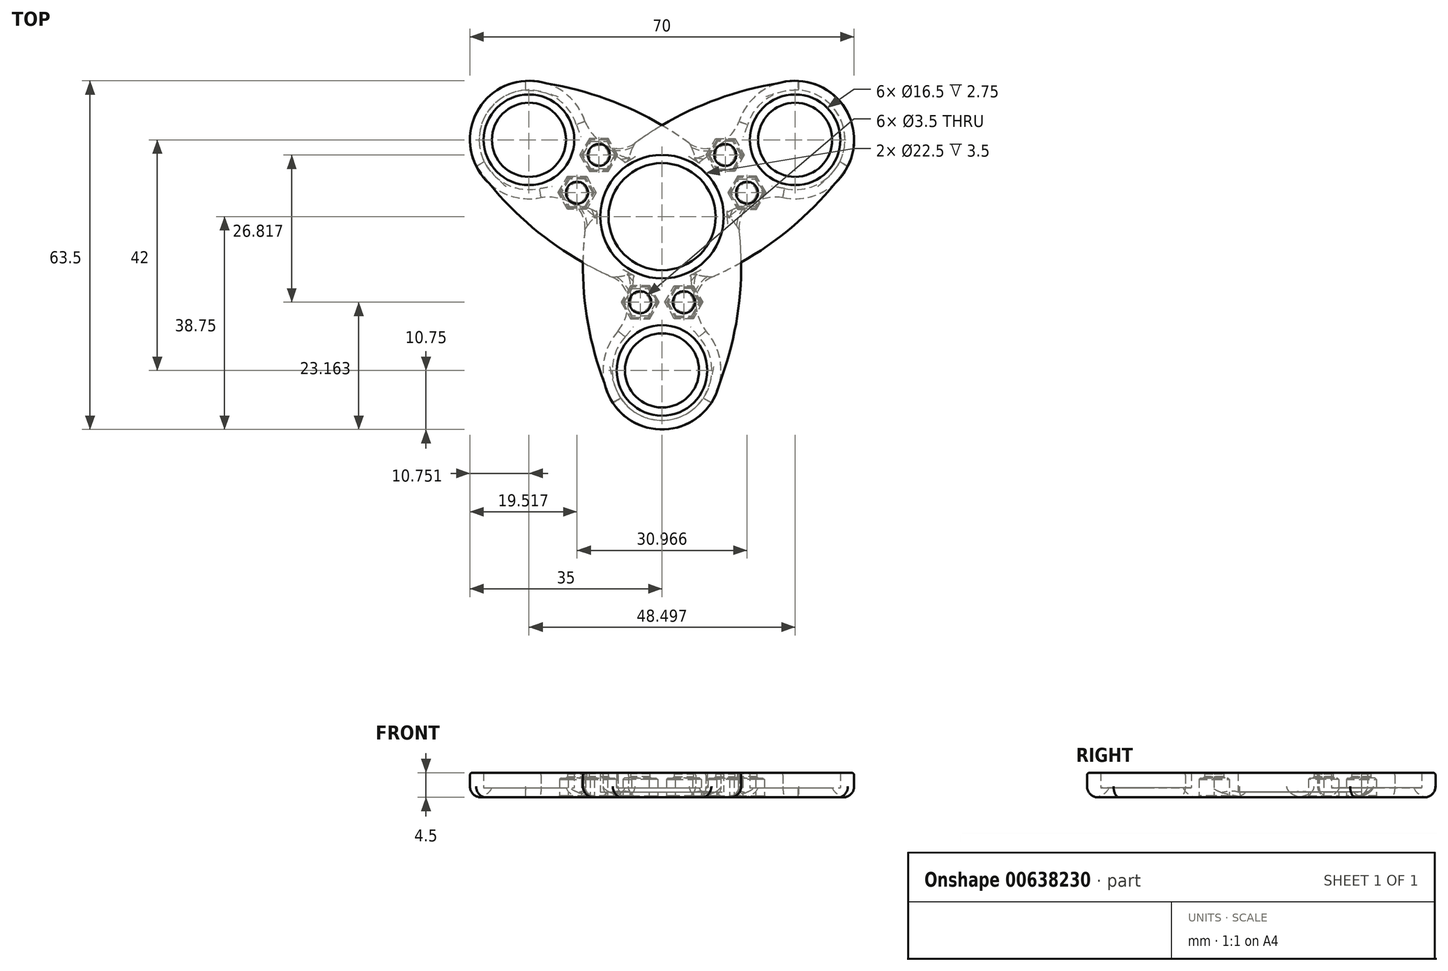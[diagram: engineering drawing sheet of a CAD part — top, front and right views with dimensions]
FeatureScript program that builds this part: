
annotation { "Feature Type Name" : "Feature", "Feature Type Description" : "" }
export const myFeature = defineFeature(function(context is Context, id is Id, definition is map)
    precondition{}
    {
        {
            assignVariable(context, id + "F0", {"name" : "OuterBearingHeight", "anyValue" : 5});
        }
        {
            assignVariable(context, id + "F1", {"name" : "CenterBearingHeight", "anyValue" : 7});
        }
        {
            var Q0;
            Q0=qCreatedBy(makeId("Top.planeOp"),FACE);
            var sketch = newSketch(context, id + "F2", { "sketchPlane" : qUnion([Q0])});
            skCircle(sketch, "E0", {"center": v(0, 0) * mm, "radius": 11.25 * mm});
            skCircle(sketch, "E1", {"center": v(0, 0) * mm, "radius": 9.75 * mm});
            skCircle(sketch, "E2", {"center": v(0, -28) * mm, "radius": 8.25 * mm});
            skCircle(sketch, "E3", {"center": v(0, -28) * mm, "radius": 6.75 * mm});
            skCircle(sketch, "E4", {"center": v(0, 0) * mm, "radius": 13.75 * mm});
            skCircle(sketch, "E5", {"center": v(0, -28) * mm, "radius": 10.75 * mm});
            skArc(sketch, "E6", {"start": v(-13.75, 0) * mm, "mid": v(-13.84, -17.29) * mm, "end": v(-9, -33.88) * mm});
            skArc(sketch, "E7", {"start": v(6.75, -11.98) * mm, "mid": v(6.2, -16.57) * mm, "end": v(8, -20.82) * mm});
            skPoint(sketch, "E8.center", {"position": v(0.04, 0.07) * mm});
            skCircle(sketch, "E9.cCircle", {"center": v(-3.97, -15.59) * mm, "radius": 2.75 * mm, "construction": true});
            skLineSegment(sketch, "E9.0", {"start": v(-2.38, -18.34) * mm, "end": v(-5.56, -18.34) * mm});
            skLineSegment(sketch, "E9.1", {"start": v(-5.56, -18.34) * mm, "end": v(-7.14, -15.59) * mm});
            skLineSegment(sketch, "E9.2", {"start": v(-7.14, -15.59) * mm, "end": v(-5.56, -12.84) * mm});
            skLineSegment(sketch, "E9.3", {"start": v(-5.56, -12.84) * mm, "end": v(-2.38, -12.84) * mm});
            skLineSegment(sketch, "E9.4", {"start": v(-2.38, -12.84) * mm, "end": v(-0.8, -15.59) * mm});
            skLineSegment(sketch, "E9.5", {"start": v(-0.8, -15.59) * mm, "end": v(-2.38, -18.34) * mm});
            skPoint(sketch, "E9.0.midPoint", {"position": v(-3.97, -18.34) * mm});
            skLineSegment(sketch, "E10", {"start": v(-3.97, -15.59) * mm, "end": v(-3.97, -13.16) * mm, "construction": true});
            skLineSegment(sketch, "E11", {"start": v(-3.97, -15.59) * mm, "end": v(-3.97, -18) * mm, "construction": true});
            skLineSegment(sketch, "E12", {"start": v(-3.97, -15.59) * mm, "end": v(-14.05, -15.59) * mm, "construction": true});
            skLineSegment(sketch, "E13", {"start": v(-3.97, -15.59) * mm, "end": v(6.12, -15.59) * mm, "construction": true});
            skCircle(sketch, "E14", {"center": v(-3.97, -15.59) * mm, "radius": 1.75 * mm});
            skArc(sketch, "E15.1.0", {"start": v(7, 11.84) * mm, "mid": v(11.25, 13.65) * mm, "end": v(14.03, 17.34) * mm});
            skCircle(sketch, "E15.1.1", {"center": v(24.25, 14) * mm, "radius": 10.75 * mm});
            skCircle(sketch, "E15.1.2", {"center": v(24.25, 14) * mm, "radius": 8.25 * mm});
            skCircle(sketch, "E15.1.3", {"center": v(24.25, 14) * mm, "radius": 6.75 * mm});
            skArc(sketch, "E15.1.4", {"start": v(6.88, -11.9) * mm, "mid": v(21.89, -3.34) * mm, "end": v(33.84, 9.15) * mm});
            skLineSegment(sketch, "E15.1.5", {"start": v(13.9, 7.1) * mm, "end": v(17.07, 7.1) * mm});
            skLineSegment(sketch, "E15.1.6", {"start": v(12.3, 4.36) * mm, "end": v(13.9, 7.1) * mm});
            skLineSegment(sketch, "E15.1.7", {"start": v(13.9, 1.6) * mm, "end": v(12.3, 4.36) * mm});
            skLineSegment(sketch, "E15.1.8", {"start": v(17.07, 1.6) * mm, "end": v(13.9, 1.6) * mm});
            skLineSegment(sketch, "E15.1.9", {"start": v(18.66, 4.36) * mm, "end": v(17.07, 1.6) * mm});
            skLineSegment(sketch, "E15.1.10", {"start": v(17.07, 7.1) * mm, "end": v(18.66, 4.36) * mm});
            skCircle(sketch, "E15.1.11", {"center": v(15.48, 4.36) * mm, "radius": 1.75 * mm});
            skArc(sketch, "E15.2.0", {"start": v(-13.75, 0.14) * mm, "mid": v(-17.45, 2.91) * mm, "end": v(-22.03, 3.48) * mm});
            skCircle(sketch, "E15.2.1", {"center": v(-24.25, 14) * mm, "radius": 10.75 * mm});
            skCircle(sketch, "E15.2.2", {"center": v(-24.25, 14) * mm, "radius": 8.25 * mm});
            skCircle(sketch, "E15.2.3", {"center": v(-24.25, 14) * mm, "radius": 6.75 * mm});
            skArc(sketch, "E15.2.4", {"start": v(6.87, 11.9) * mm, "mid": v(-8.05, 20.63) * mm, "end": v(-24.84, 24.73) * mm});
            skLineSegment(sketch, "E15.2.5", {"start": v(-13.1, 8.48) * mm, "end": v(-14.7, 11.23) * mm});
            skLineSegment(sketch, "E15.2.6", {"start": v(-9.93, 8.48) * mm, "end": v(-13.1, 8.48) * mm});
            skLineSegment(sketch, "E15.2.7", {"start": v(-8.34, 11.23) * mm, "end": v(-9.93, 8.48) * mm});
            skLineSegment(sketch, "E15.2.8", {"start": v(-9.93, 13.98) * mm, "end": v(-8.34, 11.23) * mm});
            skLineSegment(sketch, "E15.2.9", {"start": v(-13.1, 13.98) * mm, "end": v(-9.93, 13.98) * mm});
            skLineSegment(sketch, "E15.2.10", {"start": v(-14.7, 11.23) * mm, "end": v(-13.1, 13.98) * mm});
            skCircle(sketch, "E15.2.11", {"center": v(-11.51, 11.23) * mm, "radius": 1.75 * mm});
            skSolve(sketch);
        }
        {
            var Q0;
            {var subQ0=sQuery(id+"F2.wireOp",EDGE,"E9.1");Q0=makeQuery(id+"F2.imprint","IMPRINT",FACE,{"disambiguationData":[TD([[makeQuery(id+"F2.imprint","IMPRINT",EDGE,{"derivedFrom":subQ0}),1.0]])]});}
            var Q1;
            {var subQ5=sQuery(id+"F2.wireOp",EDGE,"E7");Q1=makeQuery(id+"F2.imprint","IMPRINT",FACE,{"disambiguationData":[TD([[makeQuery(id+"F2.imprint","IMPRINT",EDGE,{"derivedFrom":subQ5}),-1.0]])]});}
            var Q2;
            {var subQ0=sQuery(id+"F2.wireOp",EDGE,"E15.1.8");Q2=makeQuery(id+"F2.imprint","IMPRINT",FACE,{"disambiguationData":[TD([[makeQuery(id+"F2.imprint","IMPRINT",EDGE,{"derivedFrom":subQ0}),1.0]])]});}
            var Q3;
            Q3=makeQuery(id+"F2.imprint","IMPRINT",FACE,{"disambiguationData":[TD([[makeQuery(id+"F2.imprint","IMPRINT",EDGE,{"derivedFrom":sQuery(id+"F2.wireOp",EDGE,"E0")}),-1.0]])]});
            var Q4;
            {var subQ1=sQuery(id+"F2.wireOp",EDGE,"E15.1.0");Q4=makeQuery(id+"F2.imprint","IMPRINT",FACE,{"disambiguationData":[TD([[makeQuery(id+"F2.imprint","IMPRINT",EDGE,{"derivedFrom":subQ1}),-1.0]])]});}
            var Q5;
            {var subQ0=sQuery(id+"F2.wireOp",EDGE,"E15.2.8");Q5=makeQuery(id+"F2.imprint","IMPRINT",FACE,{"disambiguationData":[TD([[makeQuery(id+"F2.imprint","IMPRINT",EDGE,{"derivedFrom":subQ0}),1.0]])]});}
            var Q6;
            Q6=makeQuery(id+"F2.imprint","IMPRINT",FACE,{"disambiguationData":[TD([[makeQuery(id+"F2.imprint","IMPRINT",EDGE,{"derivedFrom":sQuery(id+"F2.wireOp",EDGE,"E15.2.2")}),-1.0]])]});
            var Q7;
            Q7=makeQuery(id+"F2.imprint","IMPRINT",FACE,{"disambiguationData":[TD([[makeQuery(id+"F2.imprint","IMPRINT",EDGE,{"derivedFrom":sQuery(id+"F2.wireOp",EDGE,"E15.1.2")}),-1.0]])]});
            var Q8;
            {var subQ1=sQuery(id+"F2.wireOp",EDGE,"E15.2.0");Q8=makeQuery(id+"F2.imprint","IMPRINT",FACE,{"disambiguationData":[TD([[makeQuery(id+"F2.imprint","IMPRINT",EDGE,{"derivedFrom":subQ1}),-1.0]])]});}
            var Q9;
            Q9=makeQuery(id+"F2.imprint","IMPRINT",FACE,{"disambiguationData":[TD([[makeQuery(id+"F2.imprint","IMPRINT",EDGE,{"derivedFrom":sQuery(id+"F2.wireOp",EDGE,"E2")}),-1.0]])]});
            extrude(context, id + "F3", {"entities" : qUnion([Q0, Q1, Q2, Q3, Q4, Q5, Q6, Q7, Q8, Q9]), "depth" : ((getVariable(context, 'CenterBearingHeight') / 2) + 1) * mm, "offsetDistance" : 25 * mm});
        }
        {
            var Q0;
            Q0=makeQuery(id+"F2.imprint","IMPRINT",FACE,{"disambiguationData":[TD([[makeQuery(id+"F2.imprint","IMPRINT",EDGE,{"derivedFrom":sQuery(id+"F2.wireOp",EDGE,"E15.2.2")}),1.0]])]});
            var Q1;
            Q1=makeQuery(id+"F2.imprint","IMPRINT",FACE,{"disambiguationData":[TD([[makeQuery(id+"F2.imprint","IMPRINT",EDGE,{"derivedFrom":sQuery(id+"F2.wireOp",EDGE,"E15.1.2")}),1.0]])]});
            var Q2;
            Q2=makeQuery(id+"F2.imprint","IMPRINT",FACE,{"disambiguationData":[TD([[makeQuery(id+"F2.imprint","IMPRINT",EDGE,{"derivedFrom":sQuery(id+"F2.wireOp",EDGE,"E2")}),1.0]])]});
            extrude(context, id + "F4", {"entities" : qUnion([Q0, Q1, Q2]), "operationType" : NewBodyOperationType.ADD, "depth" : (((getVariable(context, 'CenterBearingHeight') / 2) + .75) - getVariable(context, 'OuterBearingHeight') / 2) * mm, "offsetDistance" : 25 * mm});
        }
        {
            var Q0;
            {var subQ0=sQuery(id+"F2.wireOp",EDGE,"E9.1");Q0=makeQuery(id+"F2.imprint","IMPRINT",FACE,{"disambiguationData":[TD([[makeQuery(id+"F2.imprint","IMPRINT",EDGE,{"derivedFrom":subQ0}),-1.0]])]});}
            var Q1;
            {var subQ0=sQuery(id+"F2.wireOp",EDGE,"E9.3");var subQ1=sQuery(id+"F2.wireOp",EDGE,"E4");var subQ2=makeQuery(id+"F2.imprint","INTERSECT",VERTEX,{"derivedFrom":[subQ1,subQ0]});Q1=makeQuery(id+"F2.imprint","IMPRINT",FACE,{"disambiguationData":[TD([[makeQuery(id+"F2.imprint","IMPRINT",EDGE,{"disambiguationData":[TD([[subQ2,-1.0]])],"derivedFrom":subQ1}),1.0]])]});}
            var Q2;
            {var subQ0=sQuery(id+"F2.wireOp",EDGE,"E9.5");var subQ1=sQuery(id+"F2.wireOp",EDGE,"E5");var subQ2=makeQuery(id+"F2.imprint","INTERSECT",VERTEX,{"derivedFrom":[subQ1,subQ0]});Q2=makeQuery(id+"F2.imprint","IMPRINT",FACE,{"disambiguationData":[TD([[makeQuery(id+"F2.imprint","IMPRINT",EDGE,{"disambiguationData":[TD([[subQ2,-1.0]])],"derivedFrom":subQ1}),1.0]])]});}
            var Q3;
            {var subQ0=sQuery(id+"F2.wireOp",EDGE,"E15.2.7");var subQ1=sQuery(id+"F2.wireOp",EDGE,"E4");var subQ2=makeQuery(id+"F2.imprint","INTERSECT",VERTEX,{"derivedFrom":[subQ1,subQ0]});Q3=makeQuery(id+"F2.imprint","IMPRINT",FACE,{"disambiguationData":[TD([[makeQuery(id+"F2.imprint","IMPRINT",EDGE,{"disambiguationData":[TD([[subQ2,-1.0]])],"derivedFrom":subQ1}),1.0]])]});}
            var Q4;
            {var subQ11=sQuery(id+"F2.wireOp",EDGE,"E15.2.8");Q4=makeQuery(id+"F2.imprint","IMPRINT",FACE,{"disambiguationData":[TD([[makeQuery(id+"F2.imprint","IMPRINT",EDGE,{"derivedFrom":subQ11}),-1.0]])]});}
            var Q5;
            {var subQ0=sQuery(id+"F2.wireOp",EDGE,"E15.2.5");var subQ1=sQuery(id+"F2.wireOp",EDGE,"E15.2.1");var subQ2=makeQuery(id+"F2.imprint","INTERSECT",VERTEX,{"derivedFrom":[subQ1,subQ0]});Q5=makeQuery(id+"F2.imprint","IMPRINT",FACE,{"disambiguationData":[TD([[makeQuery(id+"F2.imprint","IMPRINT",EDGE,{"disambiguationData":[TD([[subQ2,-1.0]])],"derivedFrom":subQ1}),1.0]])]});}
            var Q6;
            {var subQ11=sQuery(id+"F2.wireOp",EDGE,"E15.1.8");Q6=makeQuery(id+"F2.imprint","IMPRINT",FACE,{"disambiguationData":[TD([[makeQuery(id+"F2.imprint","IMPRINT",EDGE,{"derivedFrom":subQ11}),-1.0]])]});}
            var Q7;
            {var subQ0=sQuery(id+"F2.wireOp",EDGE,"E15.1.5");var subQ1=sQuery(id+"F2.wireOp",EDGE,"E15.1.1");var subQ2=makeQuery(id+"F2.imprint","INTERSECT",VERTEX,{"derivedFrom":[subQ1,subQ0]});Q7=makeQuery(id+"F2.imprint","IMPRINT",FACE,{"disambiguationData":[TD([[makeQuery(id+"F2.imprint","IMPRINT",EDGE,{"disambiguationData":[TD([[subQ2,-1.0]])],"derivedFrom":subQ1}),1.0]])]});}
            var Q8;
            {var subQ0=sQuery(id+"F2.wireOp",EDGE,"E15.1.6");var subQ1=sQuery(id+"F2.wireOp",EDGE,"E4");var subQ2=makeQuery(id+"F2.imprint","INTERSECT",VERTEX,{"derivedFrom":[subQ1,subQ0]});Q8=makeQuery(id+"F2.imprint","IMPRINT",FACE,{"disambiguationData":[TD([[makeQuery(id+"F2.imprint","IMPRINT",EDGE,{"disambiguationData":[TD([[subQ2,1.0]])],"derivedFrom":subQ1}),1.0]])]});}
            extrude(context, id + "F5", {"entities" : qUnion([Q0, Q1, Q2, Q3, Q4, Q5, Q6, Q7, Q8]), "operationType" : NewBodyOperationType.ADD, "depth" : ((getVariable(context, 'CenterBearingHeight') / 2) + 1) * mm, "offsetDistance" : 25 * mm, "hasSecondDirection" : true, "secondDirectionOppositeDirection" : false, "secondDirectionDepth" : 3.5 * mm});
        }
        {
            var Q0;
            Q0=makeQuery(id+"F2.imprint","IMPRINT",FACE,{"disambiguationData":[TD([[makeQuery(id+"F2.imprint","IMPRINT",EDGE,{"derivedFrom":sQuery(id+"F2.wireOp",EDGE,"E0")}),1.0]])]});
            extrude(context, id + "F6", {"entities" : qUnion([Q0]), "operationType" : NewBodyOperationType.ADD, "depth" : 1 * mm, "offsetDistance" : 25 * mm});
        }
        {
            var Q0;
            Q0=makeQuery(id+"F3.opExtrude","CAP_EDGE",EDGE,{"disambiguationData":[OSD([sQuery(id+"F2.wireOp",EDGE,"E15.1.1")])],"isStart":true});
            var Q1;
            Q1=makeQuery(id+"F3.opExtrude","CAP_EDGE",EDGE,{"disambiguationData":[OSD([sQuery(id+"F2.wireOp",EDGE,"E15.1.4")])],"isStart":true});
            var Q2;
            Q2=makeQuery(id+"F3.opExtrude","CAP_EDGE",EDGE,{"disambiguationData":[OSD([sQuery(id+"F2.wireOp",EDGE,"E7")])],"isStart":true});
            var Q3;
            Q3=makeQuery(id+"F3.opExtrude","CAP_EDGE",EDGE,{"disambiguationData":[OSD([sQuery(id+"F2.wireOp",EDGE,"E5")])],"isStart":true});
            var Q4;
            Q4=makeQuery(id+"F3.opExtrude","CAP_EDGE",EDGE,{"disambiguationData":[OSD([sQuery(id+"F2.wireOp",EDGE,"E6")])],"isStart":true});
            var Q5;
            Q5=makeQuery(id+"F3.opExtrude","CAP_EDGE",EDGE,{"disambiguationData":[OSD([sQuery(id+"F2.wireOp",EDGE,"E15.2.0")])],"isStart":true});
            var Q6;
            Q6=makeQuery(id+"F3.opExtrude","CAP_EDGE",EDGE,{"disambiguationData":[OSD([sQuery(id+"F2.wireOp",EDGE,"E15.2.1")])],"isStart":true});
            var Q7;
            Q7=makeQuery(id+"F3.opExtrude","CAP_EDGE",EDGE,{"disambiguationData":[OSD([sQuery(id+"F2.wireOp",EDGE,"E15.2.4")])],"isStart":true});
            var Q8;
            Q8=makeQuery(id+"F3.opExtrude","CAP_EDGE",EDGE,{"disambiguationData":[OSD([sQuery(id+"F2.wireOp",EDGE,"E15.1.0")])],"isStart":true});
            var Q9;
            {var subQ0=sQuery(id+"F2.wireOp",EDGE,"E4");Q9=makeQuery(id+"F3.opExtrude","CAP_EDGE",EDGE,{"disambiguationData":[OSD([subQ0]),TDD([makeQuery(id+"F2.imprint","IMPRINT",EDGE,{"disambiguationData":[TD([[makeQuery(id+"F2.imprint","INTERSECT",VERTEX,{"derivedFrom":[subQ0,sQuery(id+"F2.wireOp",EDGE,"E15.1.0")]}),-1.0]])],"derivedFrom":subQ0})])],"isStart":true});}
            var Q10;
            {var subQ0=sQuery(id+"F2.wireOp",EDGE,"E4");Q10=makeQuery(id+"F3.opExtrude","CAP_EDGE",EDGE,{"disambiguationData":[OSD([subQ0]),TDD([makeQuery(id+"F2.imprint","IMPRINT",EDGE,{"disambiguationData":[TD([[makeQuery(id+"F2.imprint","INTERSECT",VERTEX,{"derivedFrom":[subQ0,sQuery(id+"F2.wireOp",EDGE,"E6")]}),1.0]])],"derivedFrom":subQ0})])],"isStart":true});}
            var Q11;
            {var subQ0=sQuery(id+"F2.wireOp",EDGE,"E4");Q11=makeQuery(id+"F3.opExtrude","CAP_EDGE",EDGE,{"disambiguationData":[OSD([subQ0]),TDD([makeQuery(id+"F2.imprint","IMPRINT",EDGE,{"disambiguationData":[TD([[makeQuery(id+"F2.imprint","INTERSECT",VERTEX,{"derivedFrom":[subQ0,sQuery(id+"F2.wireOp",EDGE,"E7")]}),-1.0]])],"derivedFrom":subQ0})])],"isStart":true});}
            fillet(context, id + "F7", {"entities" : qUnion([Q0, Q1, Q2, Q3, Q4, Q5, Q6, Q7, Q8, Q9, Q10, Q11]), "radius" : 2 * mm, "tangentPropagation" : true, "allowEdgeOverflow" : false});
        }
        {
            var Q0;
            Q0=makeQuery(id+"F4.opExtrude","CAP_EDGE",EDGE,{"disambiguationData":[OSD([sQuery(id+"F2.wireOp",EDGE,"E15.2.3")])],"isStart":true});
            var Q1;
            Q1=makeQuery(id+"F6.opExtrude","CAP_EDGE",EDGE,{"disambiguationData":[OSD([sQuery(id+"F2.wireOp",EDGE,"E1")])],"isStart":true});
            var Q2;
            Q2=makeQuery(id+"F4.opExtrude","CAP_EDGE",EDGE,{"disambiguationData":[OSD([sQuery(id+"F2.wireOp",EDGE,"E3")])],"isStart":true});
            var Q3;
            Q3=makeQuery(id+"F4.opExtrude","CAP_EDGE",EDGE,{"disambiguationData":[OSD([sQuery(id+"F2.wireOp",EDGE,"E15.1.3")])],"isStart":true});
            fillet(context, id + "F8", {"entities" : qUnion([Q0, Q1, Q2, Q3]), "radius" : 3 * mm, "tangentPropagation" : true, "allowEdgeOverflow" : false});
        }
        {
            var Q0;
            Q0=makeQuery(id+"F3.opExtrude","SWEPT_EDGE",EDGE,{"disambiguationData":[OSD([sQuery(id+"F2.wireOp",EDGE,"E4"),sQuery(id+"F2.wireOp",EDGE,"E7")])]});
            var Q1;
            Q1=makeQuery(id+"F3.opExtrude","SWEPT_EDGE",EDGE,{"disambiguationData":[OSD([sQuery(id+"F2.wireOp",EDGE,"E4"),sQuery(id+"F2.wireOp",EDGE,"E15.2.0")])]});
            var Q2;
            Q2=makeQuery(id+"F3.opExtrude","SWEPT_EDGE",EDGE,{"disambiguationData":[OSD([sQuery(id+"F2.wireOp",EDGE,"E4"),sQuery(id+"F2.wireOp",EDGE,"E15.1.0")])]});
            fillet(context, id + "F9", {"entities" : qUnion([Q0, Q1, Q2]), "radius" : 8 * mm, "tangentPropagation" : true, "allowEdgeOverflow" : false});
        }
        {
            var Q0;
            Q0=makeQuery(id+"F9.opFillet","BLEND_EDGE",EDGE,{"blendedFrom":[makeQuery(id+"F3.opExtrude","SWEPT_EDGE",EDGE,{"disambiguationData":[OSD([sQuery(id+"F2.wireOp",EDGE,"E4"),sQuery(id+"F2.wireOp",EDGE,"E15.1.0")])]}),makeQuery(id+"F3.opExtrude","SWEPT_FACE",FACE,{"disambiguationData":[OSD([sQuery(id+"F2.wireOp",EDGE,"E15.2.4")])]})],"blendedInto":[makeQuery(id+"F3.opExtrude","SWEPT_FACE",FACE,{"disambiguationData":[OSD([sQuery(id+"F2.wireOp",EDGE,"E15.2.4")])]})]});
            var Q1;
            Q1=makeQuery(id+"F9.opFillet","BLEND_EDGE",EDGE,{"blendedFrom":[makeQuery(id+"F3.opExtrude","SWEPT_EDGE",EDGE,{"disambiguationData":[OSD([sQuery(id+"F2.wireOp",EDGE,"E4"),sQuery(id+"F2.wireOp",EDGE,"E15.2.0")])]}),makeQuery(id+"F3.opExtrude","SWEPT_FACE",FACE,{"disambiguationData":[OSD([sQuery(id+"F2.wireOp",EDGE,"E6")])]})],"blendedInto":[makeQuery(id+"F3.opExtrude","SWEPT_FACE",FACE,{"disambiguationData":[OSD([sQuery(id+"F2.wireOp",EDGE,"E6")])]})]});
            var Q2;
            Q2=makeQuery(id+"F9.opFillet","BLEND_EDGE",EDGE,{"blendedFrom":[makeQuery(id+"F3.opExtrude","SWEPT_EDGE",EDGE,{"disambiguationData":[OSD([sQuery(id+"F2.wireOp",EDGE,"E4"),sQuery(id+"F2.wireOp",EDGE,"E7")])]}),makeQuery(id+"F3.opExtrude","SWEPT_FACE",FACE,{"disambiguationData":[OSD([sQuery(id+"F2.wireOp",EDGE,"E15.1.4")])]})],"blendedInto":[makeQuery(id+"F3.opExtrude","SWEPT_FACE",FACE,{"disambiguationData":[OSD([sQuery(id+"F2.wireOp",EDGE,"E15.1.4")])]})]});
            fillet(context, id + "F10", {"entities" : qUnion([Q0, Q1, Q2]), "radius" : 5 * mm, "tangentPropagation" : true, "allowEdgeOverflow" : false});
        }
        {
            var Q0;
            Q0=makeQuery(id+"F3.opExtrude","CAP_EDGE",EDGE,{"disambiguationData":[OSD([sQuery(id+"F2.wireOp",EDGE,"E9.5")])],"isStart":true});
            var Q1;
            Q1=makeQuery(id+"F3.opExtrude","CAP_EDGE",EDGE,{"disambiguationData":[OSD([sQuery(id+"F2.wireOp",EDGE,"E9.4")])],"isStart":true});
            var Q2;
            Q2=makeQuery(id+"F3.opExtrude","CAP_EDGE",EDGE,{"disambiguationData":[OSD([sQuery(id+"F2.wireOp",EDGE,"E9.3")])],"isStart":true});
            var Q3;
            Q3=makeQuery(id+"F3.opExtrude","CAP_EDGE",EDGE,{"disambiguationData":[OSD([sQuery(id+"F2.wireOp",EDGE,"E9.2")])],"isStart":true});
            var Q4;
            Q4=makeQuery(id+"F3.opExtrude","CAP_EDGE",EDGE,{"disambiguationData":[OSD([sQuery(id+"F2.wireOp",EDGE,"E9.0")])],"isStart":true});
            var Q5;
            Q5=makeQuery(id+"F3.opExtrude","CAP_EDGE",EDGE,{"disambiguationData":[OSD([sQuery(id+"F2.wireOp",EDGE,"E9.1")])],"isStart":true});
            var Q6;
            Q6=makeQuery(id+"F5.opExtrude","CAP_EDGE",EDGE,{"disambiguationData":[OSD([sQuery(id+"F2.wireOp",EDGE,"E14")])],"isStart":false});
            var Q7;
            Q7=makeQuery(id+"F5.opExtrude","CAP_EDGE",EDGE,{"disambiguationData":[OSD([sQuery(id+"F2.wireOp",EDGE,"E14")])],"isStart":true});
            var Q8;
            Q8=makeQuery(id+"F5.opExtrude","CAP_FACE",FACE,{"disambiguationData":[OSD([sQuery(id+"F2.wireOp",EDGE,"E9.0"),sQuery(id+"F2.wireOp",EDGE,"E9.1"),sQuery(id+"F2.wireOp",EDGE,"E9.2"),sQuery(id+"F2.wireOp",EDGE,"E9.3"),sQuery(id+"F2.wireOp",EDGE,"E9.4"),sQuery(id+"F2.wireOp",EDGE,"E9.5"),sQuery(id+"F2.wireOp",EDGE,"E14")])],"isStart":true});
            var Q9;
            Q9=makeQuery(id+"F5.opExtrude","CAP_FACE",FACE,{"disambiguationData":[OSD([sQuery(id+"F2.wireOp",EDGE,"E15.2.5"),sQuery(id+"F2.wireOp",EDGE,"E15.2.6"),sQuery(id+"F2.wireOp",EDGE,"E15.2.7"),sQuery(id+"F2.wireOp",EDGE,"E15.2.8"),sQuery(id+"F2.wireOp",EDGE,"E15.2.9"),sQuery(id+"F2.wireOp",EDGE,"E15.2.10"),sQuery(id+"F2.wireOp",EDGE,"E15.2.11")])],"isStart":true});
            var Q10;
            Q10=makeQuery(id+"F5.opExtrude","CAP_EDGE",EDGE,{"disambiguationData":[OSD([sQuery(id+"F2.wireOp",EDGE,"E15.2.11")])],"isStart":false});
            var Q11;
            Q11=makeQuery(id+"F3.opExtrude","CAP_EDGE",EDGE,{"disambiguationData":[OSD([sQuery(id+"F2.wireOp",EDGE,"E15.2.10")])],"isStart":true});
            var Q12;
            Q12=makeQuery(id+"F3.opExtrude","CAP_EDGE",EDGE,{"disambiguationData":[OSD([sQuery(id+"F2.wireOp",EDGE,"E15.2.9")])],"isStart":true});
            var Q13;
            Q13=makeQuery(id+"F3.opExtrude","CAP_EDGE",EDGE,{"disambiguationData":[OSD([sQuery(id+"F2.wireOp",EDGE,"E15.2.5")])],"isStart":true});
            var Q14;
            Q14=makeQuery(id+"F3.opExtrude","CAP_EDGE",EDGE,{"disambiguationData":[OSD([sQuery(id+"F2.wireOp",EDGE,"E15.2.6")])],"isStart":true});
            var Q15;
            Q15=makeQuery(id+"F3.opExtrude","CAP_EDGE",EDGE,{"disambiguationData":[OSD([sQuery(id+"F2.wireOp",EDGE,"E15.2.7")])],"isStart":true});
            var Q16;
            Q16=makeQuery(id+"F3.opExtrude","CAP_EDGE",EDGE,{"disambiguationData":[OSD([sQuery(id+"F2.wireOp",EDGE,"E15.2.8")])],"isStart":true});
            var Q17;
            Q17=makeQuery(id+"F5.opExtrude","CAP_FACE",FACE,{"disambiguationData":[OSD([sQuery(id+"F2.wireOp",EDGE,"E15.1.5"),sQuery(id+"F2.wireOp",EDGE,"E15.1.6"),sQuery(id+"F2.wireOp",EDGE,"E15.1.7"),sQuery(id+"F2.wireOp",EDGE,"E15.1.8"),sQuery(id+"F2.wireOp",EDGE,"E15.1.9"),sQuery(id+"F2.wireOp",EDGE,"E15.1.10"),sQuery(id+"F2.wireOp",EDGE,"E15.1.11")])],"isStart":true});
            var Q18;
            Q18=makeQuery(id+"F5.opExtrude","CAP_EDGE",EDGE,{"disambiguationData":[OSD([sQuery(id+"F2.wireOp",EDGE,"E15.1.11")])],"isStart":false});
            var Q19;
            Q19=makeQuery(id+"F3.opExtrude","CAP_EDGE",EDGE,{"disambiguationData":[OSD([sQuery(id+"F2.wireOp",EDGE,"E15.1.5")])],"isStart":true});
            var Q20;
            Q20=makeQuery(id+"F3.opExtrude","CAP_EDGE",EDGE,{"disambiguationData":[OSD([sQuery(id+"F2.wireOp",EDGE,"E15.1.10")])],"isStart":true});
            var Q21;
            Q21=makeQuery(id+"F3.opExtrude","CAP_EDGE",EDGE,{"disambiguationData":[OSD([sQuery(id+"F2.wireOp",EDGE,"E15.1.9")])],"isStart":true});
            var Q22;
            Q22=makeQuery(id+"F3.opExtrude","CAP_EDGE",EDGE,{"disambiguationData":[OSD([sQuery(id+"F2.wireOp",EDGE,"E15.1.8")])],"isStart":true});
            var Q23;
            Q23=makeQuery(id+"F3.opExtrude","CAP_EDGE",EDGE,{"disambiguationData":[OSD([sQuery(id+"F2.wireOp",EDGE,"E15.1.7")])],"isStart":true});
            var Q24;
            Q24=makeQuery(id+"F3.opExtrude","CAP_EDGE",EDGE,{"disambiguationData":[OSD([sQuery(id+"F2.wireOp",EDGE,"E15.1.6")])],"isStart":true});
            chamfer(context, id + "F11", {"entities" : qUnion([Q0, Q1, Q2, Q3, Q4, Q5, Q6, Q7, Q8, Q9, Q10, Q11, Q12, Q13, Q14, Q15, Q16, Q17, Q18, Q19, Q20, Q21, Q22, Q23, Q24]), "width" : .25 * mm, "tangentPropagation" : true});
        }
        {
            var Q0;
            Q0=makeQuery(id+"F3.opExtrude","SWEPT_EDGE",EDGE,{"disambiguationData":[OSD([sQuery(id+"F2.wireOp",EDGE,"E5"),sQuery(id+"F2.wireOp",EDGE,"E6")])]});
            var Q1;
            Q1=makeQuery(id+"F3.opExtrude","SWEPT_EDGE",EDGE,{"disambiguationData":[OSD([sQuery(id+"F2.wireOp",EDGE,"E15.2.1"),sQuery(id+"F2.wireOp",EDGE,"E15.2.4")])]});
            var Q2;
            Q2=makeQuery(id+"F3.opExtrude","SWEPT_EDGE",EDGE,{"disambiguationData":[OSD([sQuery(id+"F2.wireOp",EDGE,"E15.1.1"),sQuery(id+"F2.wireOp",EDGE,"E15.1.4")])]});
            var Q3;
            Q3=makeQuery(id+"F3.opExtrude","CAP_EDGE",EDGE,{"disambiguationData":[OSD([sQuery(id+"F2.wireOp",EDGE,"E5")])],"isStart":false});
            var Q4;
            Q4=makeQuery(id+"F3.opExtrude","CAP_EDGE",EDGE,{"disambiguationData":[OSD([sQuery(id+"F2.wireOp",EDGE,"E6")])],"isStart":false});
            var Q5;
            Q5=makeQuery(id+"F3.opExtrude","CAP_EDGE",EDGE,{"disambiguationData":[OSD([sQuery(id+"F2.wireOp",EDGE,"E15.1.4")])],"isStart":false});
            var Q6;
            Q6=makeQuery(id+"F3.opExtrude","CAP_EDGE",EDGE,{"disambiguationData":[OSD([sQuery(id+"F2.wireOp",EDGE,"E15.1.1")])],"isStart":false});
            var Q7;
            Q7=makeQuery(id+"F3.opExtrude","CAP_EDGE",EDGE,{"disambiguationData":[OSD([sQuery(id+"F2.wireOp",EDGE,"E15.2.4")])],"isStart":false});
            var Q8;
            Q8=makeQuery(id+"F3.opExtrude","CAP_EDGE",EDGE,{"disambiguationData":[OSD([sQuery(id+"F2.wireOp",EDGE,"E15.2.1")])],"isStart":false});
            fillet(context, id + "F12", {"entities" : qUnion([Q0, Q1, Q2, Q3, Q4, Q5, Q6, Q7, Q8]), "radius" : .5 * mm, "tangentPropagation" : true, "allowEdgeOverflow" : false});
        }
        {
            var Q0;
            Q0=makeQuery(id+"F3.opExtrude","SWEPT_BODY",BODY,{"disambiguationData":[OSD([sQuery(id+"F2.wireOp",EDGE,"E0"),sQuery(id+"F2.wireOp",EDGE,"E2"),sQuery(id+"F2.wireOp",EDGE,"E4"),sQuery(id+"F2.wireOp",EDGE,"E5"),sQuery(id+"F2.wireOp",EDGE,"E6"),sQuery(id+"F2.wireOp",EDGE,"E7"),sQuery(id+"F2.wireOp",EDGE,"E9.0"),sQuery(id+"F2.wireOp",EDGE,"E9.1"),sQuery(id+"F2.wireOp",EDGE,"E9.2"),sQuery(id+"F2.wireOp",EDGE,"E9.3"),sQuery(id+"F2.wireOp",EDGE,"E9.4"),sQuery(id+"F2.wireOp",EDGE,"E9.5"),sQuery(id+"F2.wireOp",EDGE,"E15.1.0"),sQuery(id+"F2.wireOp",EDGE,"E15.1.1"),sQuery(id+"F2.wireOp",EDGE,"E15.1.2"),sQuery(id+"F2.wireOp",EDGE,"E15.1.4"),sQuery(id+"F2.wireOp",EDGE,"E15.1.5"),sQuery(id+"F2.wireOp",EDGE,"E15.1.6"),sQuery(id+"F2.wireOp",EDGE,"E15.1.7"),sQuery(id+"F2.wireOp",EDGE,"E15.1.8"),sQuery(id+"F2.wireOp",EDGE,"E15.1.9"),sQuery(id+"F2.wireOp",EDGE,"E15.1.10"),sQuery(id+"F2.wireOp",EDGE,"E15.2.0"),sQuery(id+"F2.wireOp",EDGE,"E15.2.1"),sQuery(id+"F2.wireOp",EDGE,"E15.2.2"),sQuery(id+"F2.wireOp",EDGE,"E15.2.4"),sQuery(id+"F2.wireOp",EDGE,"E15.2.5"),sQuery(id+"F2.wireOp",EDGE,"E15.2.6"),sQuery(id+"F2.wireOp",EDGE,"E15.2.7"),sQuery(id+"F2.wireOp",EDGE,"E15.2.8"),sQuery(id+"F2.wireOp",EDGE,"E15.2.9"),sQuery(id+"F2.wireOp",EDGE,"E15.2.10")])]});
            var Q1;
            Q1=qCreatedBy(makeId("Right.planeOp"),FACE);
            mirror(context, id + "F13", {"entities" : qUnion([Q0]), "mirrorPlane" : qUnion([Q1])});
        }
    });
